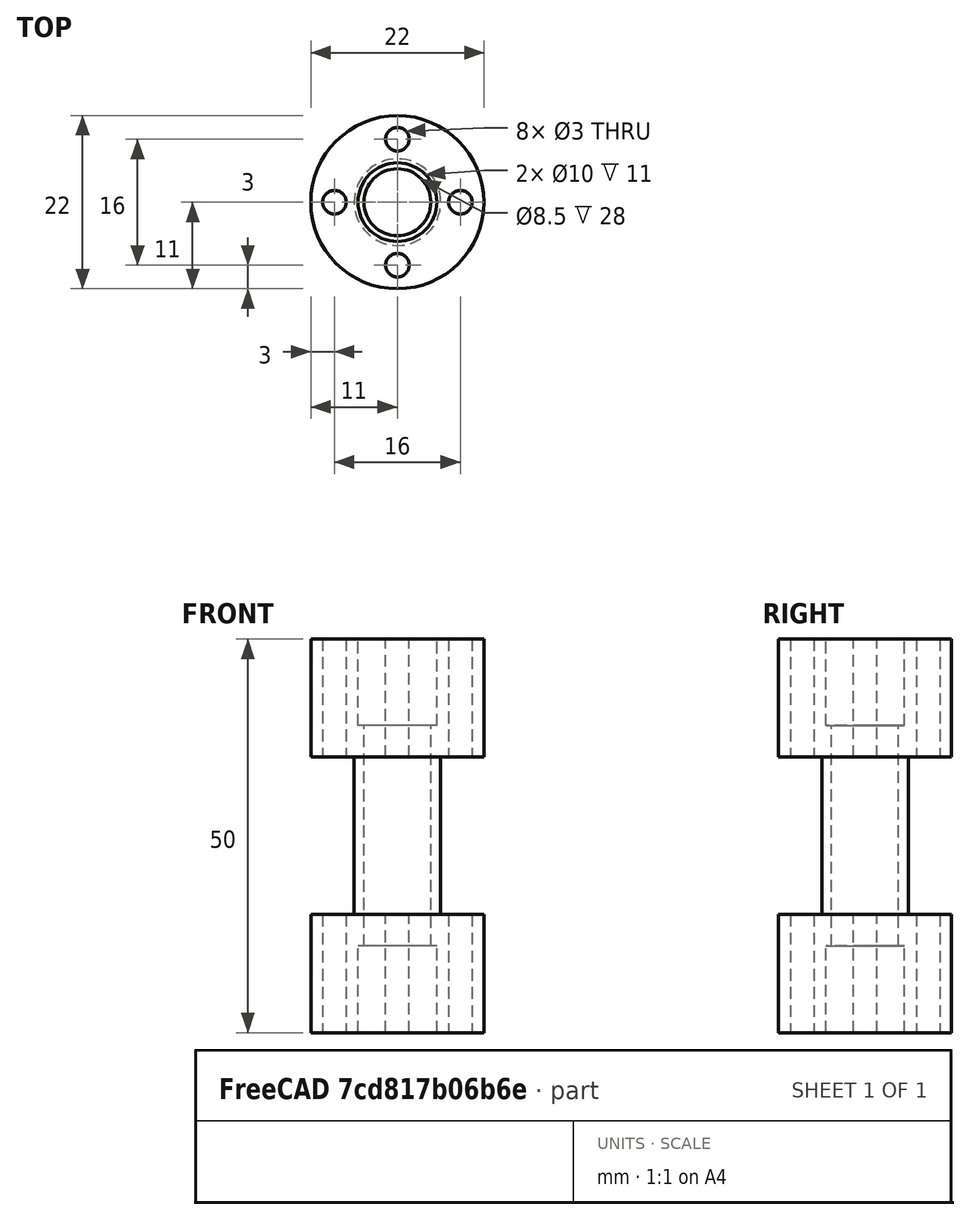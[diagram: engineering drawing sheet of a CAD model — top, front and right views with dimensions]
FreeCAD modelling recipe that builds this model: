
FCSTD DOCUMENT  (FreeCAD 0.19R)
Label: tube_assemblae_deux_vis
License: All rights reserved
LicenseURL: http://en.wikipedia.org/wiki/All_rights_reserved
objects: TechDraw::DrawViewDimension×17, TechDraw::DrawViewPart×3, Sketcher::SketchObject×2, PartDesign::Revolution×1, PartDesign::Pocket×1, PartDesign::PolarPattern×1, TechDraw::DrawSVGTemplate×1, PartDesign::Line×1, PartDesign::Body×1, TechDraw::DrawViewSection×1, TechDraw::DrawPage×1
note: 9 computed .brp shape members not serialized (recipe doc carries the construction recipe); baked Part::Feature solids carry a one-line shape summary decoded from their .brp

FEATURE [Sketcher::SketchObject] Sketch
  FullyConstrained = true
  MapMode = 5
  Placement = pos=(0,0,0) rot=(1,0,0;1.5708rad)
  Support = -> [XZ_Plane]
  sketch-geometry (12):
    g0: LineSegment StartX=5 StartY=-25 StartZ=0 EndX=5 EndY=-14 EndZ=0
    g1: LineSegment StartX=5 StartY=25 StartZ=0 EndX=11 EndY=25 EndZ=0
    g2: LineSegment StartX=11 StartY=25 StartZ=0 EndX=11 EndY=10 EndZ=0
    g3: LineSegment StartX=11 StartY=10 StartZ=0 EndX=5.5 EndY=10 EndZ=0
    g4: LineSegment StartX=5.5 StartY=10 StartZ=0 EndX=5.5 EndY=-10 EndZ=0
    g5: LineSegment StartX=5.5 StartY=-10 StartZ=0 EndX=11 EndY=-10 EndZ=0
    g6: LineSegment StartX=11 StartY=-10 StartZ=0 EndX=11 EndY=-25 EndZ=0
    g7: LineSegment StartX=11 StartY=-25 StartZ=0 EndX=5 EndY=-25 EndZ=0
    g8: LineSegment StartX=5 StartY=-14 StartZ=0 EndX=4.25 EndY=-14 EndZ=0
    g9: LineSegment StartX=4.25 StartY=-14 StartZ=0 EndX=4.25 EndY=14 EndZ=0
    g10: LineSegment StartX=4.25 StartY=14 StartZ=0 EndX=5 EndY=14 EndZ=0
    g11: LineSegment StartX=5 StartY=14 StartZ=0 EndX=5 EndY=25 EndZ=0
  constraints (34):
    c: Vertical(g0)
    c: Coincident(g11,g1)
    c: Horizontal(g1)
    c: Coincident(g1,g2)
    c: Vertical(g2)
    c: Coincident(g2,g3)
    c: Horizontal(g3)
    c: Coincident(g3,g4)
    c: Vertical(g4)
    c: Coincident(g4,g5)
    c: Horizontal(g5)
    c: Coincident(g5,g6)
    c: Vertical(g6)
    c: Coincident(g6,g7)
    c: Coincident(g7,g0)
    c: Horizontal(g7)
    c: DistanceX(g-1,g11) = 5
    c: DistanceX(g-1,g1) = 11
    c: DistanceX(g-1,g3) = 5.5
    c: DistanceY(g6,g6) = 15
    c: DistanceY(g4,g4) = 20
    c: DistanceY(g2,g2) = 15
    c: Symmetric(g1,g6,g-1)
    c: Horizontal(g8)
    c: Coincident(g8,g9)
    c: Vertical(g9)
    c: Coincident(g9,g10)
    c: Horizontal(g10)
    c: Coincident(g0,g8)
    c: Tangent(g0,g11)
    c: Coincident(g10,g11)
    c: DistanceY(g11,g11) = 11
    c: DistanceX(g10,g10) = 0.75
    c: DistanceY(g0,g0) = 11
FEATURE [PartDesign::Revolution] Revolution
  Angle = 360
  Axis = (0,-2e-16,1)
  Base = (0,0,0)
  Placement = pos=(0,0,0) rot=(1,0,0;1.5708rad)
  Profile = -> Sketch
  ReferenceAxis = -> Sketch [V_Axis]
  Reversed = true
FEATURE [Sketcher::SketchObject] Sketch001
  FullyConstrained = true
  MapMode = 5
  Placement = pos=(0,0,-14) rot=(1,0,0;3.14159rad)
  Support = -> [Revolution]
  sketch-geometry (1):
    g0: Circle CenterX=0 CenterY=8 CenterZ=0 NormalX=0 NormalY=0 NormalZ=1 AngleXU=0 Radius=1.5
  constraints (3):
    c: PointOnObject(g0,g-2)
    c: Radius(g0) = 1.5
    c: DistanceY(g-1,g0) = 8
FEATURE [PartDesign::Pocket] Pocket
  BaseFeature = -> Revolution
  Length = 5
  Length2 = 100
  Midplane = true
  Placement = pos=(0,0,0) rot=(1,0,0;1.5708rad)
  Profile = -> Sketch001
  Type = 1
FEATURE [PartDesign::PolarPattern] PolarPattern
  Angle = 360
  Axis = -> Sketch001 [N_Axis]
  BaseFeature = -> Pocket
  Occurrences = 4
  Originals = -> [Pocket]
  Placement = pos=(0,0,0) rot=(1,0,0;1.5708rad)
FEATURE [TechDraw::DrawSVGTemplate] Template
  EditableTexts = Designed_by_Name=JC Carré; Drawing_number=1/1; FC-Date=16/06/21; FC-SC=2:1; FC-SH=1/1; FC-Title=Tube assemblage vis axe Z
  Height = 210
  Orientation = 1
  Width = 297
FEATURE [PartDesign::Line] DatumLine
  AttacherType = Attacher::AttachEngineLine
  Length = 20
  MapMode = 42
  Placement = pos=(-5.2e-15,1e-16,0) rot=(0,0,1;0rad)
  ResizeMode = 0
  Support = -> [PolarPattern]
FEATURE [PartDesign::Body] Body
  Group = -> [Sketch,Revolution,Sketch001,Pocket,PolarPattern,DatumLine]
  Origin = -> Origin
  Tip = -> PolarPattern
FEATURE [TechDraw::DrawViewPart] View  label="Vue Iso"
  CoarseView = false
  Direction = (0.502,-0.73,0.465)
  Focus = 100
  HardHidden = false
  IsoCount = 0
  IsoHidden = false
  IsoVisible = false
  LockPosition = false
  Perspective = false
  Rotation = 0
  Scale = 2
  ScaleType = 0
  SeamHidden = false
  SeamVisible = true
  SmoothHidden = false
  SmoothVisible = true
  Source = -> [Body]
  X = 256.308
  XDirection = (0.81,0.585,0.044)
  Y = 130.325
FEATURE [TechDraw::DrawViewPart] View002  label="Vue de dessus"
  CoarseView = false
  Direction = (0,0,-1)
  Focus = 100
  HardHidden = false
  IsoCount = 0
  IsoHidden = false
  IsoVisible = false
  LockPosition = false
  Perspective = false
  Rotation = 0
  Scale = 2
  ScaleType = 0
  SeamHidden = false
  SeamVisible = true
  SmoothHidden = false
  SmoothVisible = true
  Source = -> [Body]
  X = 81.2618
  XDirection = (1,0,0)
  Y = 41.3735
FEATURE [TechDraw::DrawViewPart] View001  label="Vue de face"
  CoarseView = false
  Direction = (0,-1,0)
  Focus = 100
  HardHidden = false
  IsoCount = 0
  IsoHidden = false
  IsoVisible = false
  LockPosition = false
  Perspective = false
  Rotation = 0
  Scale = 2
  ScaleType = 0
  SeamHidden = false
  SeamVisible = true
  SmoothHidden = false
  SmoothVisible = true
  Source = -> [Body]
  X = 81.3849
  XDirection = (1,0,0)
  Y = 137.56
FEATURE [TechDraw::DrawViewDimension] Dimension
  Arbitrary = false
  ArbitraryTolerances = false
  EqualTolerance = true
  FormatSpec = %.0f
  FormatSpecTolerance = %+.0f
  Inverted = false
  LockPosition = false
  MeasureType = 1
  OverTolerance = 0
  References2D = -> [View001]
  Rotation = 0
  Scale = 2
  ScaleType = 0
  TheoreticalExact = false
  Type = 2
  UnderTolerance = 0
  X = -36.4993
  Y = -0.429448
FEATURE [TechDraw::DrawViewDimension] Dimension002
  Arbitrary = false
  ArbitraryTolerances = false
  EqualTolerance = true
  FormatSpec = %.0f
  FormatSpecTolerance = %+.0f
  Inverted = false
  LockPosition = false
  MeasureType = 1
  OverTolerance = 0
  References2D = -> [View001]
  Rotation = 0
  Scale = 2
  ScaleType = 0
  TheoreticalExact = false
  Type = 1
  UnderTolerance = 0
  X = -3.00614
  Y = 12.2699
FEATURE [TechDraw::DrawViewSection] SectionView  label="Section  - "
  BaseView = -> View001
  CoarseView = false
  CutSurfaceDisplay = 2
  Direction = (-1,0,0)
  FileGeomPattern = <path>
  FileHatchPattern = <path>
  Focus = 100
  FuseBeforeCut = false
  HardHidden = false
  HatchScale = 1
  IsoCount = 0
  IsoHidden = false
  IsoVisible = false
  LockPosition = false
  NameGeomPattern = Diamant
  Perspective = false
  Rotation = 0
  Scale = 2
  ScaleType = 0
  SeamHidden = false
  SeamVisible = true
  SectionDirection = 0
  SectionNormal = (-1,0,0)
  SectionOrigin = (0,0,0)
  SmoothHidden = false
  SmoothVisible = true
  Source = -> [Body]
  X = 175.051
  XDirection = (0,-1,0)
  Y = 137.636
FEATURE [TechDraw::DrawViewDimension] Dimension004
  Arbitrary = false
  ArbitraryTolerances = false
  EqualTolerance = true
  FormatSpec = %.0f
  FormatSpecTolerance = %+.0f
  Inverted = false
  LockPosition = false
  MeasureType = 1
  OverTolerance = 0
  References2D = -> [SectionView]
  Rotation = 0
  Scale = 2
  ScaleType = 0
  TheoreticalExact = false
  Type = 1
  UnderTolerance = 0
  X = -4.72194
  Y = -59.2316
FEATURE [TechDraw::DrawViewDimension] Dimension005
  Arbitrary = false
  ArbitraryTolerances = false
  EqualTolerance = true
  FormatSpec = %.0f
  FormatSpecTolerance = %+.0f
  Inverted = false
  LockPosition = false
  MeasureType = 1
  OverTolerance = 0
  References2D = -> [SectionView]
  Rotation = 0
  Scale = 2
  ScaleType = 0
  TheoreticalExact = false
  Type = 2
  UnderTolerance = 0
  X = 12.3612
  Y = 3.81141
FEATURE [TechDraw::DrawViewDimension] Dimension006
  Arbitrary = false
  ArbitraryTolerances = false
  EqualTolerance = true
  FormatSpec = %.0f
  FormatSpecTolerance = %+.0f
  Inverted = false
  LockPosition = false
  MeasureType = 1
  OverTolerance = 0
  References2D = -> [SectionView]
  Rotation = 0
  Scale = 2
  ScaleType = 0
  TheoreticalExact = false
  Type = 2
  UnderTolerance = 0
  X = 22
  Y = 35
FEATURE [TechDraw::DrawViewDimension] Dimension007
  Arbitrary = false
  ArbitraryTolerances = false
  EqualTolerance = true
  FormatSpec = %.0f
  FormatSpecTolerance = %+.0f
  Inverted = false
  LockPosition = false
  MeasureType = 1
  OverTolerance = 0
  References2D = -> [SectionView]
  Rotation = 0
  Scale = 2
  ScaleType = 0
  TheoreticalExact = false
  Type = 2
  UnderTolerance = 0
  X = 22
  Y = -35
FEATURE [TechDraw::DrawViewDimension] Dimension008
  Arbitrary = false
  ArbitraryTolerances = false
  EqualTolerance = true
  FormatSpec = %.0f
  FormatSpecTolerance = %+.0f
  Inverted = false
  LockPosition = false
  MeasureType = 1
  OverTolerance = 0
  References2D = -> [SectionView]
  Rotation = 0
  Scale = 2
  ScaleType = 0
  TheoreticalExact = false
  Type = 2
  UnderTolerance = 0
  X = -10
  Y = 39
FEATURE [TechDraw::DrawViewDimension] Dimension009
  Arbitrary = false
  ArbitraryTolerances = false
  EqualTolerance = true
  FormatSpec = %.0f
  FormatSpecTolerance = %+.0f
  Inverted = false
  LockPosition = false
  MeasureType = 1
  OverTolerance = 0
  References2D = -> [SectionView]
  Rotation = 0
  Scale = 2
  ScaleType = 0
  TheoreticalExact = false
  Type = 2
  UnderTolerance = 0
  X = -10
  Y = -39
FEATURE [TechDraw::DrawViewDimension] Dimension012
  Arbitrary = false
  ArbitraryTolerances = false
  EqualTolerance = true
  FormatSpec = ⌀%.0f
  FormatSpecTolerance = %+.0f
  Inverted = false
  LockPosition = false
  MeasureType = 1
  OverTolerance = 0
  References2D = -> [View002]
  Rotation = 0
  Scale = 2
  ScaleType = 0
  TheoreticalExact = false
  Type = 5
  UnderTolerance = 0
  X = 35.2952
  Y = -6.62525
FEATURE [TechDraw::DrawViewDimension] Dimension013
  Arbitrary = false
  ArbitraryTolerances = false
  EqualTolerance = true
  FormatSpec = ⌀%.0f
  FormatSpecTolerance = %+.0f
  Inverted = false
  LockPosition = false
  MeasureType = 1
  OverTolerance = 0
  References2D = -> [View002]
  Rotation = 0
  Scale = 2
  ScaleType = 0
  TheoreticalExact = false
  Type = 5
  UnderTolerance = 0
  X = -29.2574
  Y = -16.8557
FEATURE [TechDraw::DrawViewDimension] Dimension014
  Arbitrary = false
  ArbitraryTolerances = false
  EqualTolerance = true
  FormatSpec = ⌀%.0f
  FormatSpecTolerance = %+.0f
  Inverted = false
  LockPosition = false
  MeasureType = 1
  OverTolerance = 0
  References2D = -> [View002]
  Rotation = 0
  Scale = 2
  ScaleType = 0
  TheoreticalExact = false
  Type = 5
  UnderTolerance = 0
  X = 27.8457
  Y = 18.3538
FEATURE [TechDraw::DrawViewDimension] Dimension015
  Arbitrary = false
  ArbitraryTolerances = false
  EqualTolerance = true
  FormatSpec = ⌀%.0f
  FormatSpecTolerance = %+.0f
  Inverted = false
  LockPosition = false
  MeasureType = 1
  OverTolerance = 0
  References2D = -> [View002]
  Rotation = 0
  Scale = 2
  ScaleType = 0
  TheoreticalExact = false
  Type = 5
  UnderTolerance = 0
  X = 25.9124
  Y = -17.1666
FEATURE [TechDraw::DrawViewDimension] Dimension016
  Arbitrary = false
  ArbitraryTolerances = false
  EqualTolerance = true
  FormatSpec = %.0f
  FormatSpecTolerance = %+.0f
  Inverted = false
  LockPosition = false
  MeasureType = 1
  OverTolerance = 0
  References2D = -> [SectionView]
  Rotation = 0
  Scale = 2
  ScaleType = 0
  TheoreticalExact = false
  Type = 1
  UnderTolerance = 0
  X = -25.8878
  Y = -3.6389
FEATURE [TechDraw::DrawViewDimension] Dimension017
  Arbitrary = false
  ArbitraryTolerances = false
  EqualTolerance = true
  FormatSpec = %.0f
  FormatSpecTolerance = %+.0f
  Inverted = false
  LockPosition = false
  MeasureType = 1
  OverTolerance = 0
  References2D = -> [View001]
  Rotation = 0
  Scale = 2
  ScaleType = 0
  TheoreticalExact = false
  Type = 1
  UnderTolerance = 0
  X = -48.6708
  Y = -52.1472
FEATURE [TechDraw::DrawViewDimension] Dimension018
  Arbitrary = false
  ArbitraryTolerances = false
  EqualTolerance = true
  FormatSpec = %.0f
  FormatSpecTolerance = %+.0f
  Inverted = false
  LockPosition = false
  MeasureType = 1
  OverTolerance = 0
  References2D = -> [SectionView]
  Rotation = 0
  Scale = 2
  ScaleType = 0
  TheoreticalExact = false
  Type = 1
  UnderTolerance = 0
  X = -5.09933
  Y = -67.8201
FEATURE [TechDraw::DrawViewDimension] Dimension019
  Arbitrary = false
  ArbitraryTolerances = false
  EqualTolerance = true
  FormatSpec = %.0f
  FormatSpecTolerance = %+.0f
  Inverted = false
  LockPosition = false
  MeasureType = 1
  OverTolerance = 0
  References2D = -> [SectionView]
  Rotation = 0
  Scale = 2
  ScaleType = 0
  TheoreticalExact = false
  Type = 1
  UnderTolerance = 0
  X = -8.9e-15
  Y = 28
FEATURE [TechDraw::DrawViewDimension] Dimension020
  Arbitrary = false
  ArbitraryTolerances = false
  EqualTolerance = true
  FormatSpec = %.0f
  FormatSpecTolerance = %+.0f
  Inverted = false
  LockPosition = false
  MeasureType = 1
  OverTolerance = 0
  References2D = -> [View002]
  Rotation = 0
  Scale = 2
  ScaleType = 0
  TheoreticalExact = false
  Type = 2
  UnderTolerance = 0
  X = -39.0528
  Y = 9.67152
FEATURE [TechDraw::DrawPage] Page
  KeepUpdated = true
  NextBalloonIndex = 1
  ProjectionType = 0
  Scale = 2
  Template = -> Template
  Views = -> [View,View001,View002,Dimension,Dimension002,SectionView,Dimension004,Dimension005,Dimension006,Dimension007,Dimension008,Dimension009,Dimension012,Dimension013,Dimension014,Dimension015,Dimension016,Dimension017,Dimension018,Dimension019,Dimension020]
note: 2 file-system paths scrubbed to <path> (originals preserved in the JSON sidecar)
